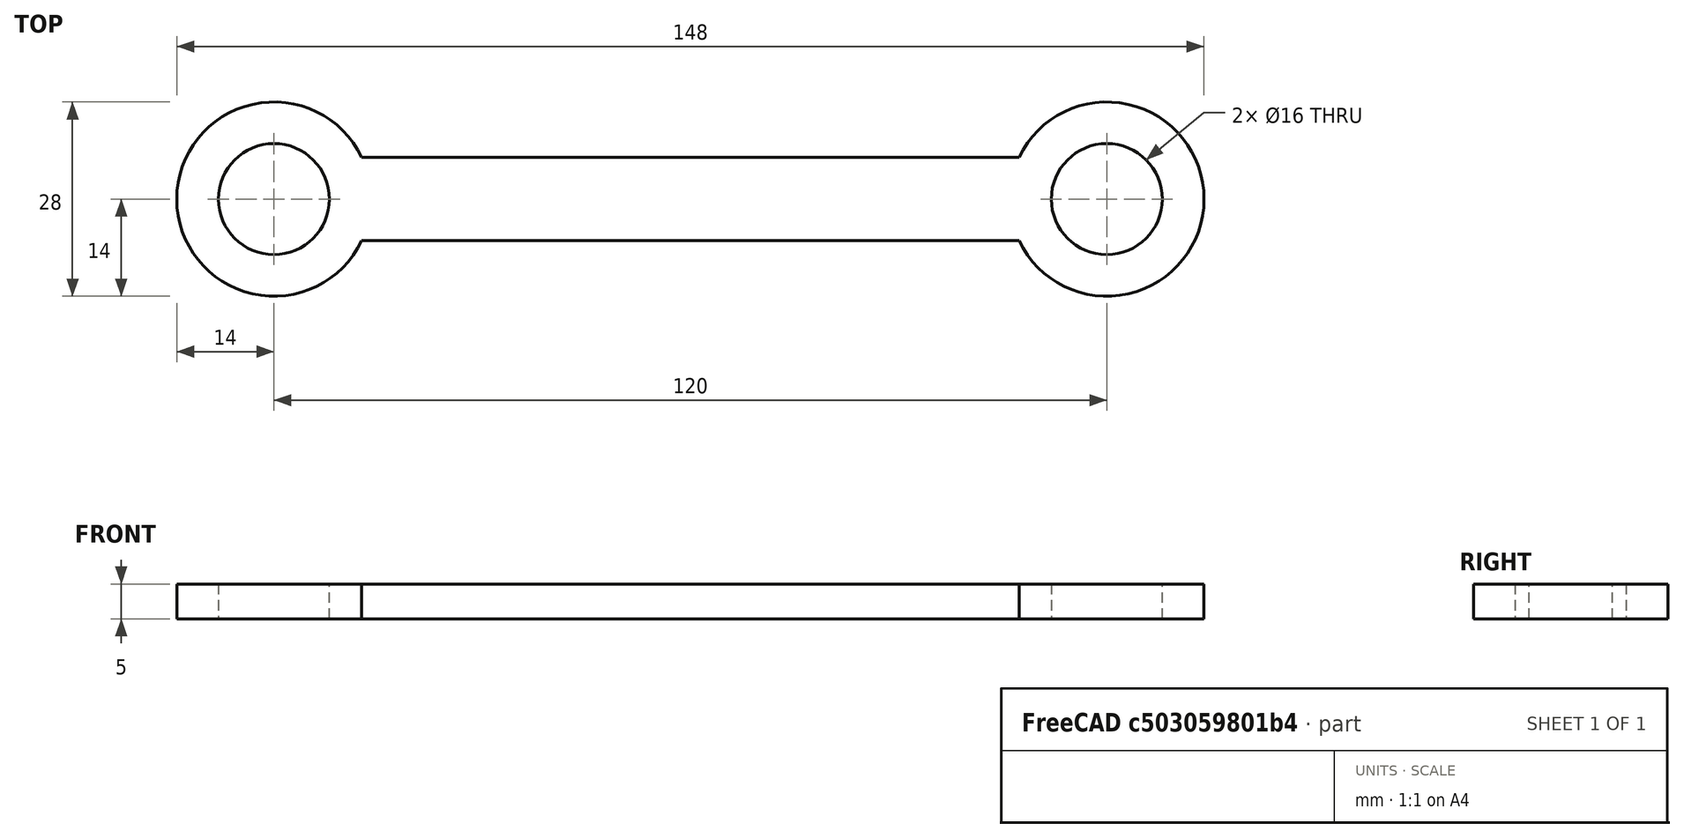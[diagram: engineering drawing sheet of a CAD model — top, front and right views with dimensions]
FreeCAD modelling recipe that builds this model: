
FCSTD DOCUMENT  (FreeCAD 0.19R24276 (Git))
Label: Knife_holder_v2
License: All rights reserved
LicenseURL: http://en.wikipedia.org/wiki/All_rights_reserved
objects: Sketcher::SketchObject×2, PartDesign::Pad×1, PartDesign::Body×1
note: 5 computed .brp shape members not serialized (recipe doc carries the construction recipe); baked Part::Feature solids carry a one-line shape summary decoded from their .brp

FEATURE [Sketcher::SketchObject] Sketch
  FullyConstrained = false
  MapMode = 5
  Support = -> [XY_Plane]
  sketch-geometry (7):
    g0: Circle CenterX=0 CenterY=0 CenterZ=0 NormalX=0 NormalY=0 NormalZ=1 AngleXU=0 Radius=8
    g1: ArcOfCircle CenterX=0 CenterY=0 CenterZ=0 NormalX=0 NormalY=0 NormalZ=1 AngleXU=0 Radius=14 StartAngle=3.5845 EndAngle=8.98187
    g2: Circle CenterX=-120 CenterY=0 CenterZ=0 NormalX=0 NormalY=0 NormalZ=1 AngleXU=0 Radius=8
    g3: ArcOfCircle CenterX=-120 CenterY=0 CenterZ=0 NormalX=0 NormalY=0 NormalZ=1 AngleXU=0 Radius=14 StartAngle=0.442911 EndAngle=5.84027
    g4: LineSegment StartX=-107.351 StartY=6 StartZ=0 EndX=-12.6491 EndY=6 EndZ=0
    g5: LineSegment StartX=-12.6491 StartY=-6 StartZ=0 EndX=-107.351 EndY=-6 EndZ=0
    g6: LineSegment StartX=0 StartY=0 StartZ=0 EndX=-60 EndY=0 EndZ=0
  constraints (19):
    c: Coincident(g0,g-1)
    c: Diameter(g0) = 16
    c: Coincident(g1,g0)
    c: Diameter(g1) = 28
    c: PointOnObject(g2,g-1)
    c: Equal(g0,g2)
    c: Coincident(g3,g2)
    c: Equal(g3,g1)
    c: DistanceX(g2,g0) = 120
    c: Horizontal(g4)
    c: Horizontal(g5)
    c: Coincident(g6,g0)
    c: PointOnObject(g6,g-1)
    c: DistanceX(g6,g6) = 60
    c: DistanceY(g5,g4) = 12
    c: Coincident(g3,g4)
    c: Coincident(g3,g5)
    c: Coincident(g1,g4)
    c: Coincident(g1,g5)
FEATURE [PartDesign::Pad] Pad
  Direction = (1,1,1)
  Length = 5
  Length2 = 100
  Profile = -> Sketch
  Type = 0
FEATURE [Sketcher::SketchObject] Sketch001
  FullyConstrained = true
  MapMode = 5
  Placement = pos=(0,0,5) rot=(0,0,1;0rad)
  Support = -> [Pad]
FEATURE [PartDesign::Body] Body
  Group = -> [Sketch,Pad,Sketch001]
  Origin = -> Origin
  Tip = -> Pad
